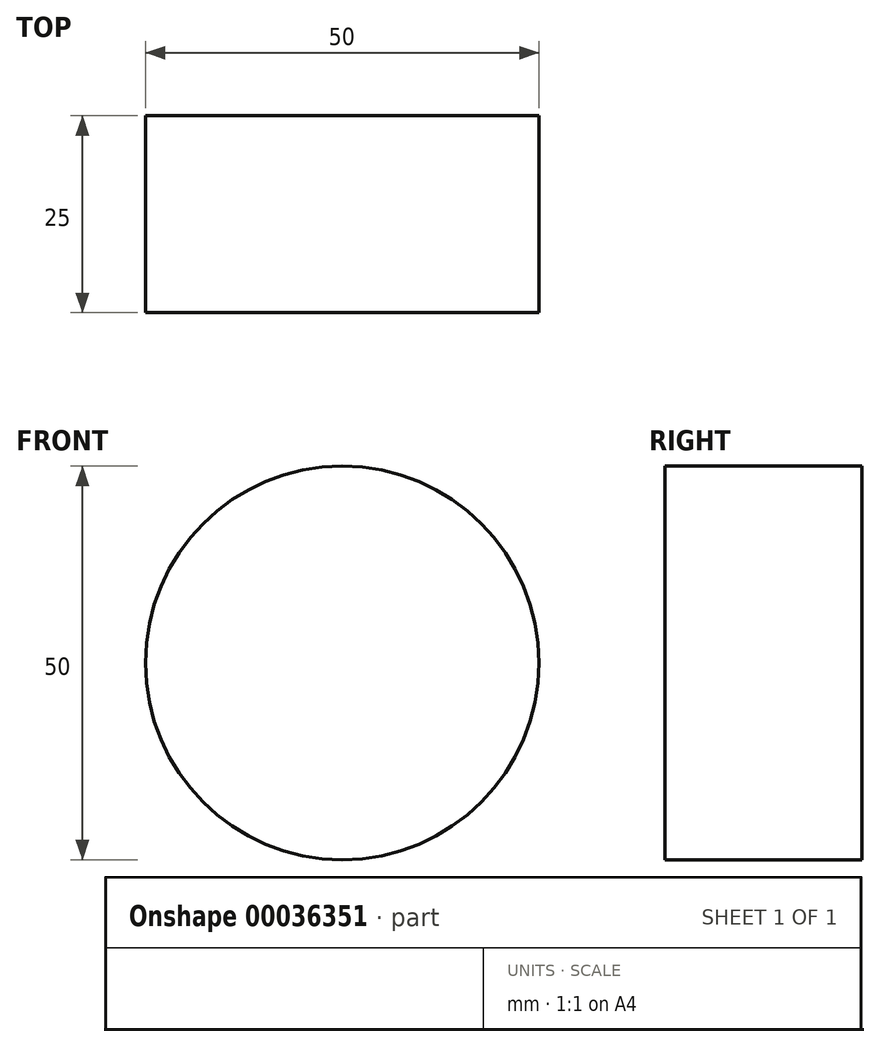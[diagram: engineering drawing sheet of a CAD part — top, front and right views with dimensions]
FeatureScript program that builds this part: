
annotation { "Feature Type Name" : "Feature", "Feature Type Description" : "" }
export const myFeature = defineFeature(function(context is Context, id is Id, definition is map)
    precondition{}
    {
        {
            var Q0;
            Q0=qCreatedBy(makeId("Front.planeOp"),FACE);
            var sketch = newSketch(context, id + "F0", { "sketchPlane" : qUnion([Q0])});
            skCircle(sketch, "E0", {"center": v(0, 0) * mm, "radius": 25 * mm});
            skSolve(sketch);
        }
        {
            var Q0;
            Q0 = qSketchRegion(id + "F0", true);
            var Q1;
            Q1=sQuery(id+"F0.wireOp",EDGE,"E0");
            extrude(context, id + "F1", {"entities" : qUnion([Q0]), "bodyType" : ToolBodyType.SURFACE, "operationType" : NewBodyOperationType.ADD, "surfaceEntities" : qUnion([Q1]), "depth" : 25 * mm});
        }
    });
